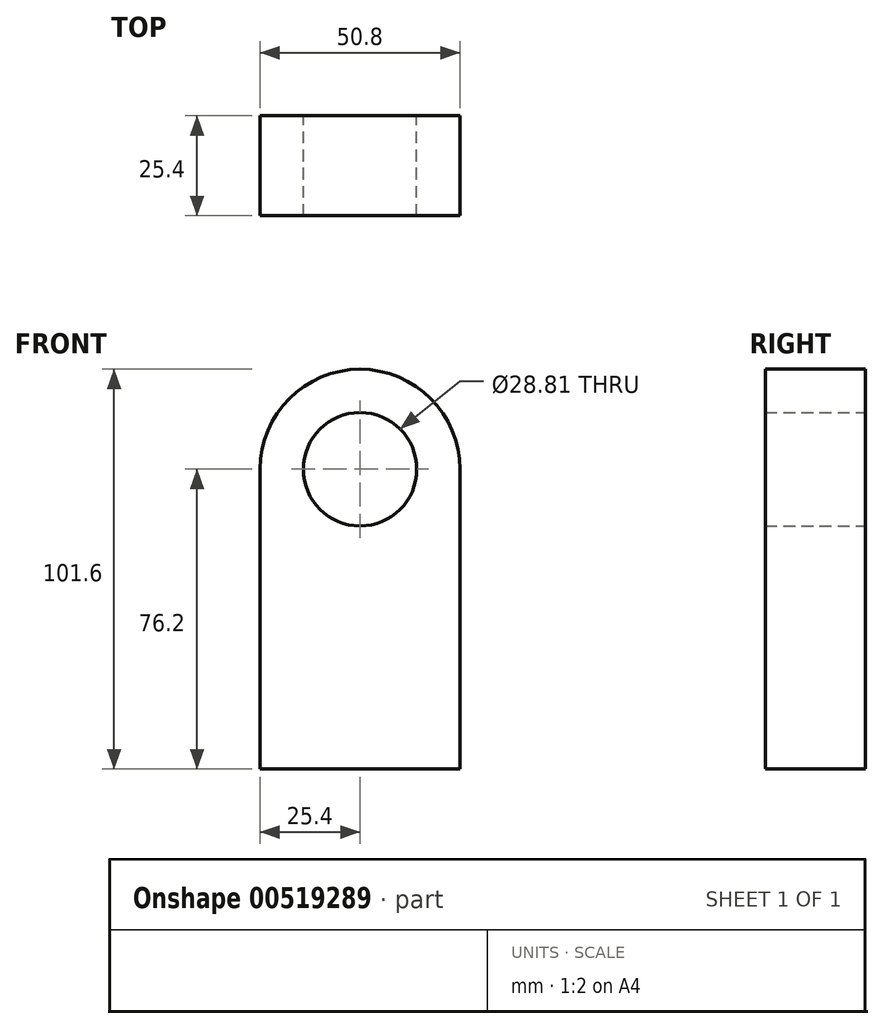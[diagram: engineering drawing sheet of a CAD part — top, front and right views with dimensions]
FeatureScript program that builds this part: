
annotation { "Feature Type Name" : "Feature", "Feature Type Description" : "" }
export const myFeature = defineFeature(function(context is Context, id is Id, definition is map)
    precondition{}
    {
        {
            var Q0;
            Q0=qCreatedBy(makeId("Front.planeOp"),FACE);
            var sketch = newSketch(context, id + "F0", { "sketchPlane" : qUnion([Q0])});
            skLineSegment(sketch, "E0.top", {"start": v(25.4, -38.1) * mm, "end": v(-25.4, -38.1) * mm});
            skLineSegment(sketch, "E0.left", {"start": v(25.4, 38.1) * mm, "end": v(25.4, -38.1) * mm});
            skLineSegment(sketch, "E0.right", {"start": v(-25.4, 38.1) * mm, "end": v(-25.4, -38.1) * mm});
            skPoint(sketch, "E0.middle", {"position": v(0, 0) * mm});
            skArc(sketch, "E1", {"start": v(25.4, 38.1) * mm, "mid": v(0, 63.5) * mm, "end": v(-25.4, 38.1) * mm});
            skCircle(sketch, "E2", {"center": v(0, 38.1) * mm, "radius": 14.4 * mm});
            skSolve(sketch);
        }
        {
            var Q0;
            Q0 = qSketchRegion(id + "F0", true);
            extrude(context, id + "F1", {"entities" : qUnion([Q0]), "depth" : 25.4 * mm, "offsetDistance" : 25.4 * mm});
        }
    });
